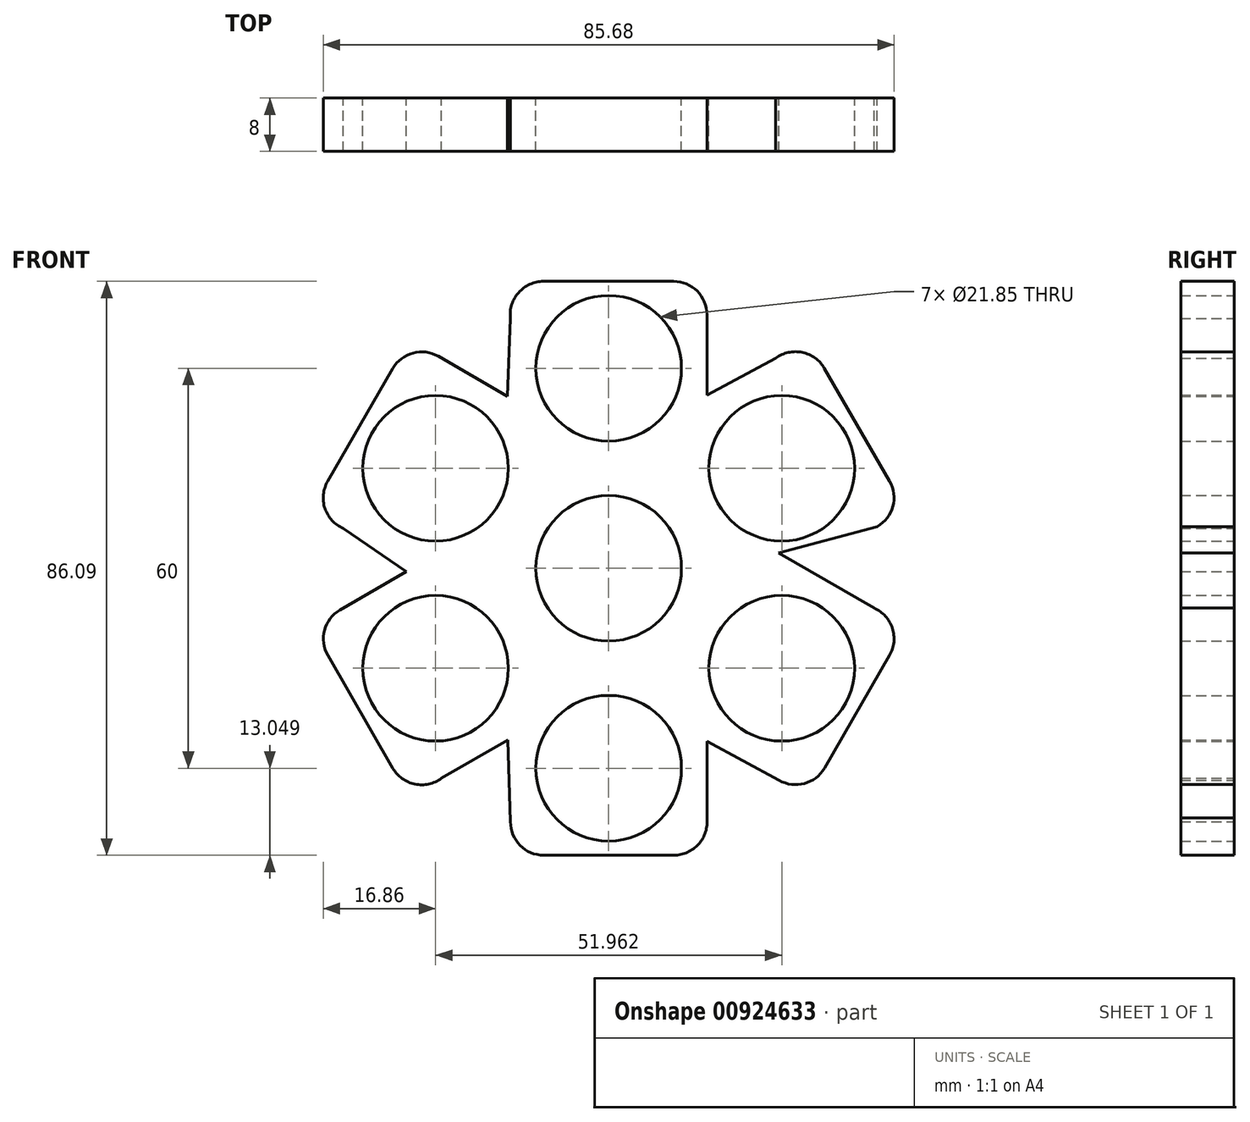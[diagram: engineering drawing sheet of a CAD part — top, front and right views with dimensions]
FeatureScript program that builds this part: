
annotation { "Feature Type Name" : "Feature", "Feature Type Description" : "" }
export const myFeature = defineFeature(function(context is Context, id is Id, definition is map)
    precondition{}
    {
        {
            var Q0;
            Q0=qCreatedBy(makeId("Front.planeOp"),FACE);
            var sketch = newSketch(context, id + "F0", { "sketchPlane" : qUnion([Q0])});
            skCircle(sketch, "E0", {"center": v(-179.2, 71.24) * mm, "radius": 10.93 * mm});
            skCircle(sketch, "E1", {"center": v(-179.2, 101.24) * mm, "radius": 10.93 * mm});
            skLineSegment(sketch, "E2", {"start": v(-179.2, 101.24) * mm, "end": v(-179.2, 71.24) * mm, "construction": true});
            skPoint(sketch, "E3", {"position": v(-179.2, 86.24) * mm});
            skLineSegment(sketch, "E4.top", {"start": v(-169.46, 114.28) * mm, "end": v(-188.99, 114.28) * mm});
            skPoint(sketch, "E5.visualSharp", {"position": v(-193.96, 114.28) * mm});
            skArc(sketch, "E5.filletArc", {"start": v(-188.99, 114.28) * mm, "mid": v(-192.72, 112.62) * mm, "end": v(-193.96, 108.72) * mm});
            skPoint(sketch, "E6.visualSharp", {"position": v(-164.46, 114.28) * mm});
            skArc(sketch, "E6.filletArc", {"start": v(-164.46, 109.28) * mm, "mid": v(-165.93, 112.82) * mm, "end": v(-169.46, 114.28) * mm});
            skPoint(sketch, "E7.1.0", {"position": v(-223.86, 80) * mm});
            skPoint(sketch, "E7.1.1", {"position": v(-209.11, 105.53) * mm});
            skPoint(sketch, "E7.1.2", {"position": v(-192.2, 78.74) * mm});
            skCircle(sketch, "E7.1.3", {"center": v(-205.19, 86.24) * mm, "radius": 10.93 * mm});
            skLineSegment(sketch, "E7.1.7", {"start": v(-211.61, 101.2) * mm, "end": v(-221.38, 84.3) * mm});
            skLineSegment(sketch, "E7.1.9", {"start": v(-205.19, 86.24) * mm, "end": v(-179.2, 71.24) * mm, "construction": true});
            skPoint(sketch, "E7.1.10", {"position": v(-192.2, 78.74) * mm});
            skArc(sketch, "E7.1.11", {"start": v(-204.78, 103.03) * mm, "mid": v(-208.58, 103.53) * mm, "end": v(-211.61, 101.2) * mm});
            skArc(sketch, "E7.1.12", {"start": v(-221.38, 84.3) * mm, "mid": v(-221.8, 80.23) * mm, "end": v(-219.04, 77.2) * mm});
            skPoint(sketch, "E7.2.0", {"position": v(-209.11, 36.94) * mm});
            skPoint(sketch, "E7.2.1", {"position": v(-223.86, 62.49) * mm});
            skPoint(sketch, "E7.2.2", {"position": v(-192.2, 63.74) * mm});
            skCircle(sketch, "E7.2.3", {"center": v(-205.19, 56.24) * mm, "radius": 10.93 * mm});
            skLineSegment(sketch, "E7.2.7", {"start": v(-221.36, 58.16) * mm, "end": v(-211.6, 41.25) * mm});
            skLineSegment(sketch, "E7.2.9", {"start": v(-205.19, 56.24) * mm, "end": v(-194.2, 62.58) * mm, "construction": true});
            skPoint(sketch, "E7.2.10", {"position": v(-192.2, 63.74) * mm});
            skArc(sketch, "E7.2.11", {"start": v(-219.53, 64.99) * mm, "mid": v(-221.86, 61.95) * mm, "end": v(-221.36, 58.16) * mm});
            skArc(sketch, "E7.2.12", {"start": v(-211.6, 41.25) * mm, "mid": v(-208.29, 38.85) * mm, "end": v(-204.3, 39.73) * mm});
            skPoint(sketch, "E8.1.3.0", {"position": v(-193.96, 28.2) * mm});
            skPoint(sketch, "E8.2.3.0", {"position": v(-179.2, 56.24) * mm});
            skCircle(sketch, "E8.3.3.0", {"center": v(-179.2, 41.24) * mm, "radius": 10.93 * mm});
            skPoint(sketch, "E8.8.3.0", {"position": v(-164.46, 28.2) * mm});
            skLineSegment(sketch, "E8.13.3.0", {"start": v(-188.96, 28.2) * mm, "end": v(-169.43, 28.2) * mm});
            skLineSegment(sketch, "E8.19.3.0", {"start": v(-179.2, 41.24) * mm, "end": v(-179.2, 71.24) * mm, "construction": true});
            skPoint(sketch, "E8.22.3.0", {"position": v(-179.2, 56.24) * mm});
            skArc(sketch, "E8.23.3.0", {"start": v(-193.96, 33.2) * mm, "mid": v(-192.5, 29.66) * mm, "end": v(-188.96, 28.2) * mm});
            skArc(sketch, "E8.27.3.0", {"start": v(-169.43, 28.2) * mm, "mid": v(-165.7, 29.86) * mm, "end": v(-164.46, 33.76) * mm});
            skPoint(sketch, "E8.1.4.0", {"position": v(-149.3, 36.94) * mm});
            skPoint(sketch, "E8.2.4.0", {"position": v(-166.22, 63.74) * mm});
            skCircle(sketch, "E8.3.4.0", {"center": v(-153.23, 56.24) * mm, "radius": 10.93 * mm});
            skPoint(sketch, "E8.8.4.0", {"position": v(-134.56, 62.49) * mm});
            skLineSegment(sketch, "E8.13.4.0", {"start": v(-146.8, 41.27) * mm, "end": v(-137.04, 58.19) * mm});
            skLineSegment(sketch, "E8.19.4.0", {"start": v(-153.23, 56.24) * mm, "end": v(-179.2, 71.24) * mm, "construction": true});
            skPoint(sketch, "E8.22.4.0", {"position": v(-166.22, 63.74) * mm});
            skArc(sketch, "E8.23.4.0", {"start": v(-153.63, 39.44) * mm, "mid": v(-149.84, 38.95) * mm, "end": v(-146.8, 41.27) * mm});
            skArc(sketch, "E8.27.4.0", {"start": v(-137.04, 58.19) * mm, "mid": v(-136.62, 62.25) * mm, "end": v(-139.37, 65.27) * mm});
            skPoint(sketch, "E8.1.5.0", {"position": v(-134.56, 80) * mm});
            skPoint(sketch, "E8.2.5.0", {"position": v(-166.22, 78.74) * mm});
            skCircle(sketch, "E8.3.5.0", {"center": v(-153.23, 86.24) * mm, "radius": 10.93 * mm});
            skPoint(sketch, "E8.8.5.0", {"position": v(-149.3, 105.53) * mm});
            skLineSegment(sketch, "E8.13.5.0", {"start": v(-137.06, 84.32) * mm, "end": v(-146.82, 101.23) * mm});
            skLineSegment(sketch, "E8.19.5.0", {"start": v(-153.23, 86.24) * mm, "end": v(-179.2, 71.24) * mm, "construction": true});
            skPoint(sketch, "E8.22.5.0", {"position": v(-166.22, 78.74) * mm});
            skArc(sketch, "E8.23.5.0", {"start": v(-138.89, 77.5) * mm, "mid": v(-136.56, 80.53) * mm, "end": v(-137.06, 84.32) * mm});
            skArc(sketch, "E8.27.5.0", {"start": v(-146.82, 101.23) * mm, "mid": v(-150.13, 103.63) * mm, "end": v(-154.12, 102.75) * mm});
            skLineSegment(sketch, "E9.trimOffspring", {"start": v(-209.56, 70.75) * mm, "end": v(-219.53, 64.99) * mm});
            skLineSegment(sketch, "E10.trimOffspring", {"start": v(-209.56, 70.75) * mm, "end": v(-219.04, 77.2) * mm});
            skLineSegment(sketch, "E11.trimOffspring", {"start": v(-192.2, 63.74) * mm, "end": v(-179.2, 71.24) * mm, "construction": true});
            skLineSegment(sketch, "E12.trimOffspring", {"start": v(-194.32, 45.49) * mm, "end": v(-193.96, 33.2) * mm});
            skLineSegment(sketch, "E13.trimOffspring", {"start": v(-194.32, 45.49) * mm, "end": v(-204.3, 39.73) * mm});
            skLineSegment(sketch, "E14.trimOffspring", {"start": v(-164.46, 45.26) * mm, "end": v(-153.63, 39.44) * mm});
            skPoint(sketch, "E15.orphan", {"position": v(-175.29, 51.94) * mm});
            skLineSegment(sketch, "E16.trimOffspring", {"start": v(-153.71, 73.55) * mm, "end": v(-138.89, 77.5) * mm});
            skLineSegment(sketch, "E17.trimOffspring", {"start": v(-194.2, 62.58) * mm, "end": v(-193.96, 58.2) * mm});
            skLineSegment(sketch, "E18.trimOffspring", {"start": v(-194.42, 97.05) * mm, "end": v(-193.96, 108.72) * mm});
            skLineSegment(sketch, "E19.trimOffspring", {"start": v(-164.46, 97.22) * mm, "end": v(-154.12, 102.75) * mm});
            skLineSegment(sketch, "E20.trimOffspring", {"start": v(-194.42, 97.05) * mm, "end": v(-204.78, 103.03) * mm});
            skLineSegment(sketch, "E21.trimOffspring", {"start": v(-164.46, 45.26) * mm, "end": v(-164.46, 33.76) * mm});
            skPoint(sketch, "E22.orphan", {"position": v(-164.46, 58.2) * mm});
            skLineSegment(sketch, "E23.trimOffspring", {"start": v(-164.46, 97.22) * mm, "end": v(-164.46, 109.28) * mm});
            skLineSegment(sketch, "E24.trimOffspring", {"start": v(-160.54, 77.49) * mm, "end": v(-139.37, 65.27) * mm});
            skSolve(sketch);
        }
        {
            var Q0;
            Q0 = qSketchRegion(id + "F0", true);
            var Q1;
            Q1=makeQuery(id+"F0.imprint","IMPRINT",FACE,{"disambiguationData":[TD([[makeQuery(id+"F0.imprint","IMPRINT",EDGE,{"derivedFrom":sQuery(id+"F0.wireOp",EDGE,"E0")}),-1.0]])]});
            var Q2;
            {var subQ0=sQuery(id+"F0.wireOp",EDGE,"E7.1.5");var subQ1=sQuery(id+"F0.wireOp",EDGE,"E4.left");var subQ2=makeQuery(id+"F0.imprint","INTERSECT",VERTEX,{"derivedFrom":[subQ1,subQ0]});Q2=makeQuery(id+"F0.imprint","IMPRINT",FACE,{"disambiguationData":[TD([[makeQuery(id+"F0.imprint","IMPRINT",EDGE,{"disambiguationData":[TD([[subQ2,-1.0]])],"derivedFrom":subQ1}),-1.0]])]});}
            var Q3;
            {var subQ0=sQuery(id+"F0.wireOp",EDGE,"E4.left");var subQ1=sQuery(id+"F0.wireOp",EDGE,"E4.bottom");var subQ2=makeQuery(id+"F0.imprint","INTERSECT",VERTEX,{"derivedFrom":[subQ1,subQ0]});Q3=makeQuery(id+"F0.imprint","IMPRINT",FACE,{"disambiguationData":[TD([[makeQuery(id+"F0.imprint","IMPRINT",EDGE,{"disambiguationData":[TD([[subQ2,-1.0]])],"derivedFrom":subQ1}),-1.0]])]});}
            var Q4;
            {var subQ0=sQuery(id+"F0.wireOp",EDGE,"E4.right");var subQ1=sQuery(id+"F0.wireOp",EDGE,"E4.bottom");var subQ2=makeQuery(id+"F0.imprint","INTERSECT",VERTEX,{"derivedFrom":[subQ1,subQ0]});Q4=makeQuery(id+"F0.imprint","IMPRINT",FACE,{"disambiguationData":[TD([[makeQuery(id+"F0.imprint","IMPRINT",EDGE,{"disambiguationData":[TD([[subQ2,1.0]])],"derivedFrom":subQ1}),-1.0]])]});}
            var Q5;
            {var subQ0=sQuery(id+"F0.wireOp",EDGE,"E7.2.6");var subQ1=sQuery(id+"F0.wireOp",EDGE,"E4.right");var subQ2=makeQuery(id+"F0.imprint","INTERSECT",VERTEX,{"derivedFrom":[subQ1,subQ0]});Q5=makeQuery(id+"F0.imprint","IMPRINT",FACE,{"disambiguationData":[TD([[makeQuery(id+"F0.imprint","IMPRINT",EDGE,{"disambiguationData":[TD([[subQ2,-1.0]])],"derivedFrom":subQ1}),1.0]])]});}
            var Q6;
            {var subQ0=sQuery(id+"F0.wireOp",EDGE,"E7.2.5");var subQ1=sQuery(id+"F0.wireOp",EDGE,"E7.1.6");var subQ2=makeQuery(id+"F0.imprint","INTERSECT",VERTEX,{"derivedFrom":[subQ1,subQ0]});Q6=makeQuery(id+"F0.imprint","IMPRINT",FACE,{"disambiguationData":[TD([[makeQuery(id+"F0.imprint","IMPRINT",EDGE,{"disambiguationData":[TD([[subQ2,-1.0]])],"derivedFrom":subQ1}),-1.0]])]});}
            var Q7;
            {var subQ0=sQuery(id+"F0.wireOp",EDGE,"E7.1.8");var subQ1=sQuery(id+"F0.wireOp",EDGE,"E7.1.6");var subQ2=makeQuery(id+"F0.imprint","INTERSECT",VERTEX,{"derivedFrom":[subQ1,subQ0]});Q7=makeQuery(id+"F0.imprint","IMPRINT",FACE,{"disambiguationData":[TD([[makeQuery(id+"F0.imprint","IMPRINT",EDGE,{"disambiguationData":[TD([[subQ2,-1.0]])],"derivedFrom":subQ1}),1.0]])]});}
            var Q8;
            Q8=makeQuery(id+"F0.imprint","IMPRINT",FACE,{"disambiguationData":[TD([[makeQuery(id+"F0.imprint","IMPRINT",EDGE,{"derivedFrom":sQuery(id+"F0.wireOp",EDGE,"E0")}),-1.0]])]});
            var Q9;
            {var subQ5=sQuery(id+"F0.wireOp",EDGE,"E8.7.4.0");var subQ6=sQuery(id+"F0.wireOp",EDGE,"E7.2.8");var subQ7=makeQuery(id+"F0.imprint","INTERSECT",VERTEX,{"derivedFrom":[subQ6,subQ5]});Q9=makeQuery(id+"F0.imprint","IMPRINT",FACE,{"disambiguationData":[TD([[makeQuery(id+"F0.imprint","IMPRINT",EDGE,{"disambiguationData":[TD([[subQ7,-1.0]])],"derivedFrom":subQ6}),-1.0]])]});}
            var Q10;
            {var subQ0=sQuery(id+"F0.wireOp",EDGE,"E8.7.5.0");var subQ1=sQuery(id+"F0.wireOp",EDGE,"E7.2.8");var subQ2=makeQuery(id+"F0.imprint","INTERSECT",VERTEX,{"derivedFrom":[subQ1,subQ0]});Q10=makeQuery(id+"F0.imprint","IMPRINT",FACE,{"disambiguationData":[TD([[makeQuery(id+"F0.imprint","IMPRINT",EDGE,{"disambiguationData":[TD([[subQ2,-1.0]])],"derivedFrom":subQ1}),-1.0]])]});}
            var Q11;
            {var subQ1=sQuery(id+"F0.wireOp",EDGE,"E8.7.4.0");var subQ3=sQuery(id+"F0.wireOp",EDGE,"E8.7.5.0");var subQ4=makeQuery(id+"F0.imprint","INTERSECT",VERTEX,{"derivedFrom":[subQ1,subQ3]});Q11=makeQuery(id+"F0.imprint","IMPRINT",FACE,{"disambiguationData":[TD([[makeQuery(id+"F0.imprint","IMPRINT",EDGE,{"disambiguationData":[TD([[subQ4,1.0]])],"derivedFrom":subQ3}),1.0]])]});}
            var Q12;
            {var subQ5=sQuery(id+"F0.wireOp",EDGE,"E8.7.5.0");var subQ7=sQuery(id+"F0.wireOp",EDGE,"E8.10.3.0");var subQ8=makeQuery(id+"F0.imprint","INTERSECT",VERTEX,{"derivedFrom":[subQ7,subQ5]});Q12=makeQuery(id+"F0.imprint","IMPRINT",FACE,{"disambiguationData":[TD([[makeQuery(id+"F0.imprint","IMPRINT",EDGE,{"disambiguationData":[TD([[subQ8,-1.0]])],"derivedFrom":subQ7}),1.0]])]});}
            var Q13;
            {var subQ1=sQuery(id+"F0.wireOp",EDGE,"E4.bottom");var subQ5=sQuery(id+"F0.wireOp",EDGE,"E8.16.5.0");var subQ6=makeQuery(id+"F0.imprint","INTERSECT",VERTEX,{"derivedFrom":[subQ1,subQ5]});Q13=makeQuery(id+"F0.imprint","IMPRINT",FACE,{"disambiguationData":[TD([[makeQuery(id+"F0.imprint","IMPRINT",EDGE,{"disambiguationData":[TD([[subQ6,-1.0]])],"derivedFrom":subQ1}),-1.0]])]});}
            var Q14;
            {var subQ1=sQuery(id+"F0.wireOp",EDGE,"E7.1.8");var subQ7=sQuery(id+"F0.wireOp",EDGE,"E4.bottom");var subQ8=makeQuery(id+"F0.imprint","INTERSECT",VERTEX,{"derivedFrom":[subQ7,subQ1]});Q14=makeQuery(id+"F0.imprint","IMPRINT",FACE,{"disambiguationData":[TD([[makeQuery(id+"F0.imprint","IMPRINT",EDGE,{"disambiguationData":[TD([[subQ8,-1.0]])],"derivedFrom":subQ7}),1.0]])]});}
            var Q15;
            {var subQ3=sQuery(id+"F0.wireOp",EDGE,"E8.10.5.0");var subQ6=sQuery(id+"F0.wireOp",EDGE,"E4.bottom");var subQ9=makeQuery(id+"F0.imprint","INTERSECT",VERTEX,{"derivedFrom":[subQ6,subQ3]});Q15=makeQuery(id+"F0.imprint","IMPRINT",FACE,{"disambiguationData":[TD([[makeQuery(id+"F0.imprint","IMPRINT",EDGE,{"disambiguationData":[TD([[subQ9,-1.0]])],"derivedFrom":subQ6}),-1.0]])]});}
            var Q16;
            {var subQ5=sQuery(id+"F0.wireOp",EDGE,"E8.7.3.0");var subQ6=sQuery(id+"F0.wireOp",EDGE,"E7.1.8");var subQ7=makeQuery(id+"F0.imprint","INTERSECT",VERTEX,{"derivedFrom":[subQ6,subQ5]});Q16=makeQuery(id+"F0.imprint","IMPRINT",FACE,{"disambiguationData":[TD([[makeQuery(id+"F0.imprint","IMPRINT",EDGE,{"disambiguationData":[TD([[subQ7,-1.0]])],"derivedFrom":subQ6}),-1.0]])]});}
            var Q17;
            {var subQ1=sQuery(id+"F0.wireOp",EDGE,"E8.10.3.0");var subQ3=sQuery(id+"F0.wireOp",EDGE,"E8.7.5.0");var subQ4=makeQuery(id+"F0.imprint","INTERSECT",VERTEX,{"derivedFrom":[subQ1,subQ3]});Q17=makeQuery(id+"F0.imprint","IMPRINT",FACE,{"disambiguationData":[TD([[makeQuery(id+"F0.imprint","IMPRINT",EDGE,{"disambiguationData":[TD([[subQ4,-1.0]])],"derivedFrom":subQ3}),1.0]])]});}
            var Q18;
            {var subQ0=sQuery(id+"F0.wireOp",EDGE,"E8.16.4.0");var subQ1=sQuery(id+"F0.wireOp",EDGE,"E8.10.3.0");var subQ2=makeQuery(id+"F0.imprint","INTERSECT",VERTEX,{"derivedFrom":[subQ1,subQ0]});Q18=makeQuery(id+"F0.imprint","IMPRINT",FACE,{"disambiguationData":[TD([[makeQuery(id+"F0.imprint","IMPRINT",EDGE,{"disambiguationData":[TD([[subQ2,-1.0]])],"derivedFrom":subQ1}),-1.0]])]});}
            var Q19;
            {var subQ0=sQuery(id+"F0.wireOp",EDGE,"E8.16.5.0");var subQ1=sQuery(id+"F0.wireOp",EDGE,"E8.10.4.0");var subQ2=makeQuery(id+"F0.imprint","INTERSECT",VERTEX,{"derivedFrom":[subQ1,subQ0]});Q19=makeQuery(id+"F0.imprint","IMPRINT",FACE,{"disambiguationData":[TD([[makeQuery(id+"F0.imprint","IMPRINT",EDGE,{"disambiguationData":[TD([[subQ2,-1.0]])],"derivedFrom":subQ1}),-1.0]])]});}
            var Q20;
            {var subQ0=sQuery(id+"F0.wireOp",EDGE,"E8.10.5.0");var subQ1=sQuery(id+"F0.wireOp",EDGE,"E7.2.8");var subQ2=makeQuery(id+"F0.imprint","INTERSECT",VERTEX,{"derivedFrom":[subQ1,subQ0]});Q20=makeQuery(id+"F0.imprint","IMPRINT",FACE,{"disambiguationData":[TD([[makeQuery(id+"F0.imprint","IMPRINT",EDGE,{"disambiguationData":[TD([[subQ2,1.0]])],"derivedFrom":subQ1}),-1.0]])]});}
            var Q21;
            {var subQ1=sQuery(id+"F0.wireOp",EDGE,"E8.7.3.0");var subQ3=sQuery(id+"F0.wireOp",EDGE,"E8.7.4.0");var subQ4=makeQuery(id+"F0.imprint","INTERSECT",VERTEX,{"derivedFrom":[subQ1,subQ3]});Q21=makeQuery(id+"F0.imprint","IMPRINT",FACE,{"disambiguationData":[TD([[makeQuery(id+"F0.imprint","IMPRINT",EDGE,{"disambiguationData":[TD([[subQ4,1.0]])],"derivedFrom":subQ3}),1.0]])]});}
            var Q22;
            {var subQ0=sQuery(id+"F0.wireOp",EDGE,"E8.7.5.0");var subQ1=sQuery(id+"F0.wireOp",EDGE,"E8.10.3.0");var subQ2=makeQuery(id+"F0.imprint","INTERSECT",VERTEX,{"derivedFrom":[subQ1,subQ0]});Q22=makeQuery(id+"F0.imprint","IMPRINT",FACE,{"disambiguationData":[TD([[makeQuery(id+"F0.imprint","IMPRINT",EDGE,{"disambiguationData":[TD([[subQ2,-1.0]])],"derivedFrom":subQ1}),-1.0]])]});}
            var Q23;
            {var subQ0=sQuery(id+"F0.wireOp",EDGE,"E8.10.4.0");var subQ1=sQuery(id+"F0.wireOp",EDGE,"E7.1.8");var subQ2=makeQuery(id+"F0.imprint","INTERSECT",VERTEX,{"derivedFrom":[subQ1,subQ0]});Q23=makeQuery(id+"F0.imprint","IMPRINT",FACE,{"disambiguationData":[TD([[makeQuery(id+"F0.imprint","IMPRINT",EDGE,{"disambiguationData":[TD([[subQ2,1.0]])],"derivedFrom":subQ1}),-1.0]])]});}
            var Q24;
            {var subQ0=sQuery(id+"F0.wireOp",EDGE,"E8.7.4.0");var subQ1=sQuery(id+"F0.wireOp",EDGE,"E7.1.8");var subQ2=makeQuery(id+"F0.imprint","INTERSECT",VERTEX,{"derivedFrom":[subQ1,subQ0]});Q24=makeQuery(id+"F0.imprint","IMPRINT",FACE,{"disambiguationData":[TD([[makeQuery(id+"F0.imprint","IMPRINT",EDGE,{"disambiguationData":[TD([[subQ2,-1.0]])],"derivedFrom":subQ1}),-1.0]])]});}
            extrude(context, id + "F1", {"entities" : qUnion([Q0, Q1, Q2, Q3, Q4, Q5, Q6, Q7, Q8, Q9, Q10, Q11, Q12, Q13, Q14, Q15, Q16, Q17, Q18, Q19, Q20, Q21, Q22, Q23, Q24]), "depth" : 8 * mm, "offsetDistance" : 25 * mm});
        }
    });
